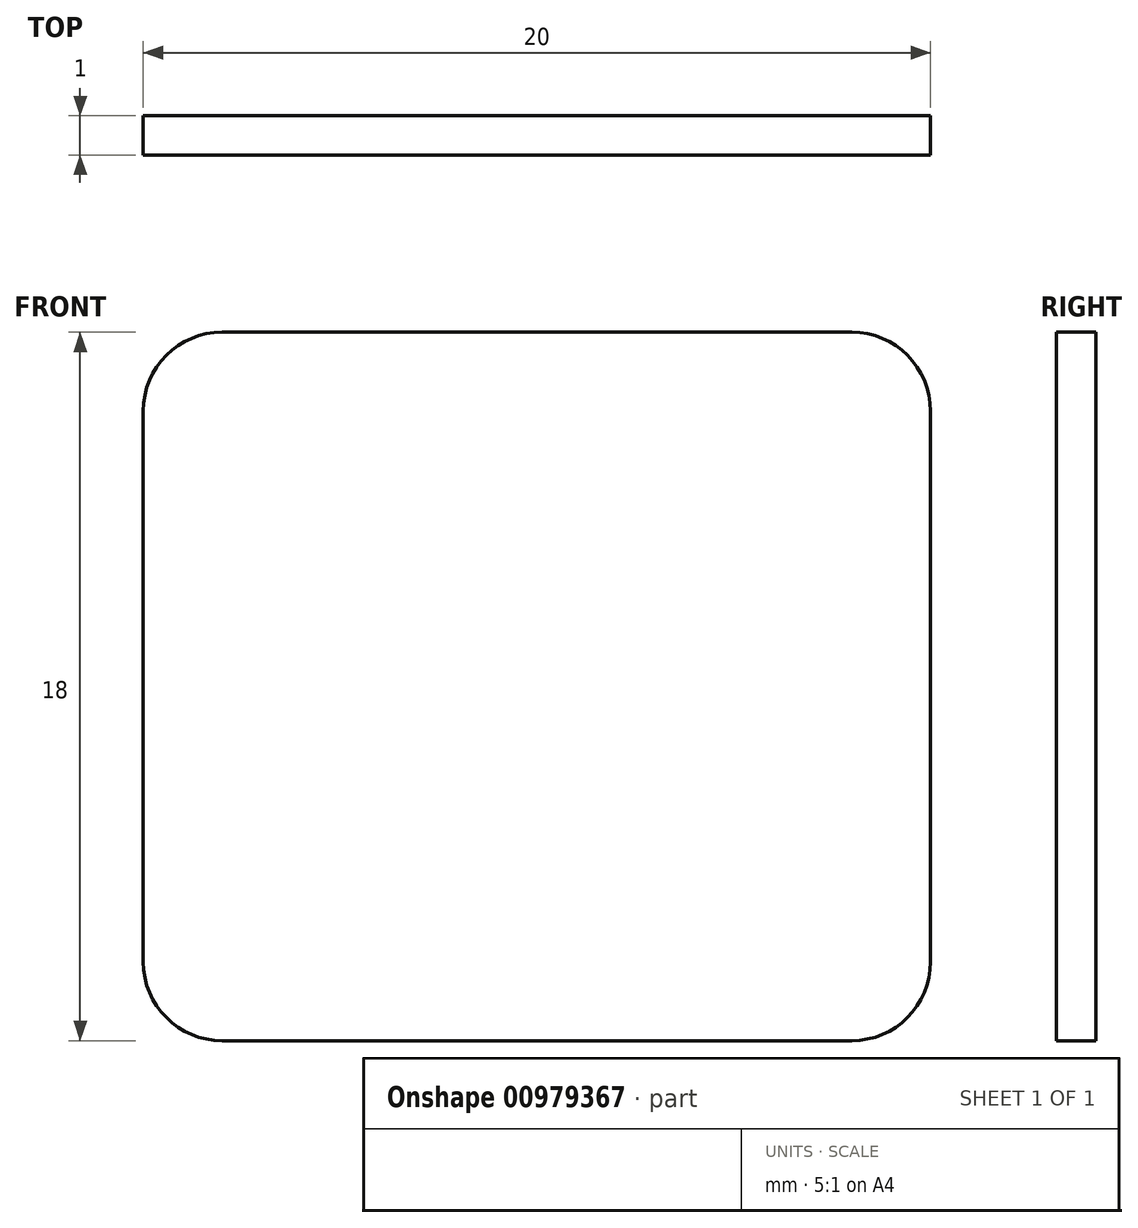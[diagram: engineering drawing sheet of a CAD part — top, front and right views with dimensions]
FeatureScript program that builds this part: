
annotation { "Feature Type Name" : "Feature", "Feature Type Description" : "" }
export const myFeature = defineFeature(function(context is Context, id is Id, definition is map)
    precondition{}
    {
        {
            var Q0;
            Q0=qCreatedBy(makeId("Front.planeOp"),FACE);
            var sketch = newSketch(context, id + "F0", { "sketchPlane" : qUnion([Q0])});
            skLineSegment(sketch, "E0.bottom", {"start": v(-10, 9) * mm, "end": v(10, 9) * mm});
            skLineSegment(sketch, "E0.top", {"start": v(-10, -9) * mm, "end": v(10, -9) * mm});
            skLineSegment(sketch, "E0.left", {"start": v(-10, 9) * mm, "end": v(-10, -9) * mm});
            skLineSegment(sketch, "E0.right", {"start": v(10, 9) * mm, "end": v(10, -9) * mm});
            skSolve(sketch);
        }
        {
            var Q0;
            Q0 = qSketchRegion(id + "F0", true);
            extrude(context, id + "F1", {"entities" : qUnion([Q0]), "depth" : 1 * mm, "offsetDistance" : 25 * mm});
        }
        {
            var Q0;
            Q0=makeQuery(id+"F1.opExtrude","SWEPT_EDGE",EDGE,{"disambiguationData":[OSD([sQuery(id+"F0.wireOp",EDGE,"E0.bottom"),sQuery(id+"F0.wireOp",EDGE,"E0.right")])]});
            var Q1;
            Q1=makeQuery(id+"F1.opExtrude","SWEPT_EDGE",EDGE,{"disambiguationData":[OSD([sQuery(id+"F0.wireOp",EDGE,"E0.top"),sQuery(id+"F0.wireOp",EDGE,"E0.right")])]});
            var Q2;
            Q2=makeQuery(id+"F1.opExtrude","SWEPT_EDGE",EDGE,{"disambiguationData":[OSD([sQuery(id+"F0.wireOp",EDGE,"E0.top"),sQuery(id+"F0.wireOp",EDGE,"E0.left")])]});
            var Q3;
            Q3=makeQuery(id+"F1.opExtrude","SWEPT_EDGE",EDGE,{"disambiguationData":[OSD([sQuery(id+"F0.wireOp",EDGE,"E0.bottom"),sQuery(id+"F0.wireOp",EDGE,"E0.left")])]});
            fillet(context, id + "F2", {"entities" : qUnion([Q0, Q1, Q2, Q3]), "tangentPropagation" : true, "radius" : 2 * mm, "defaultsChanged" : true, "vertexSettings" : [], "allowEdgeOverflow" : false});
        }
    });
